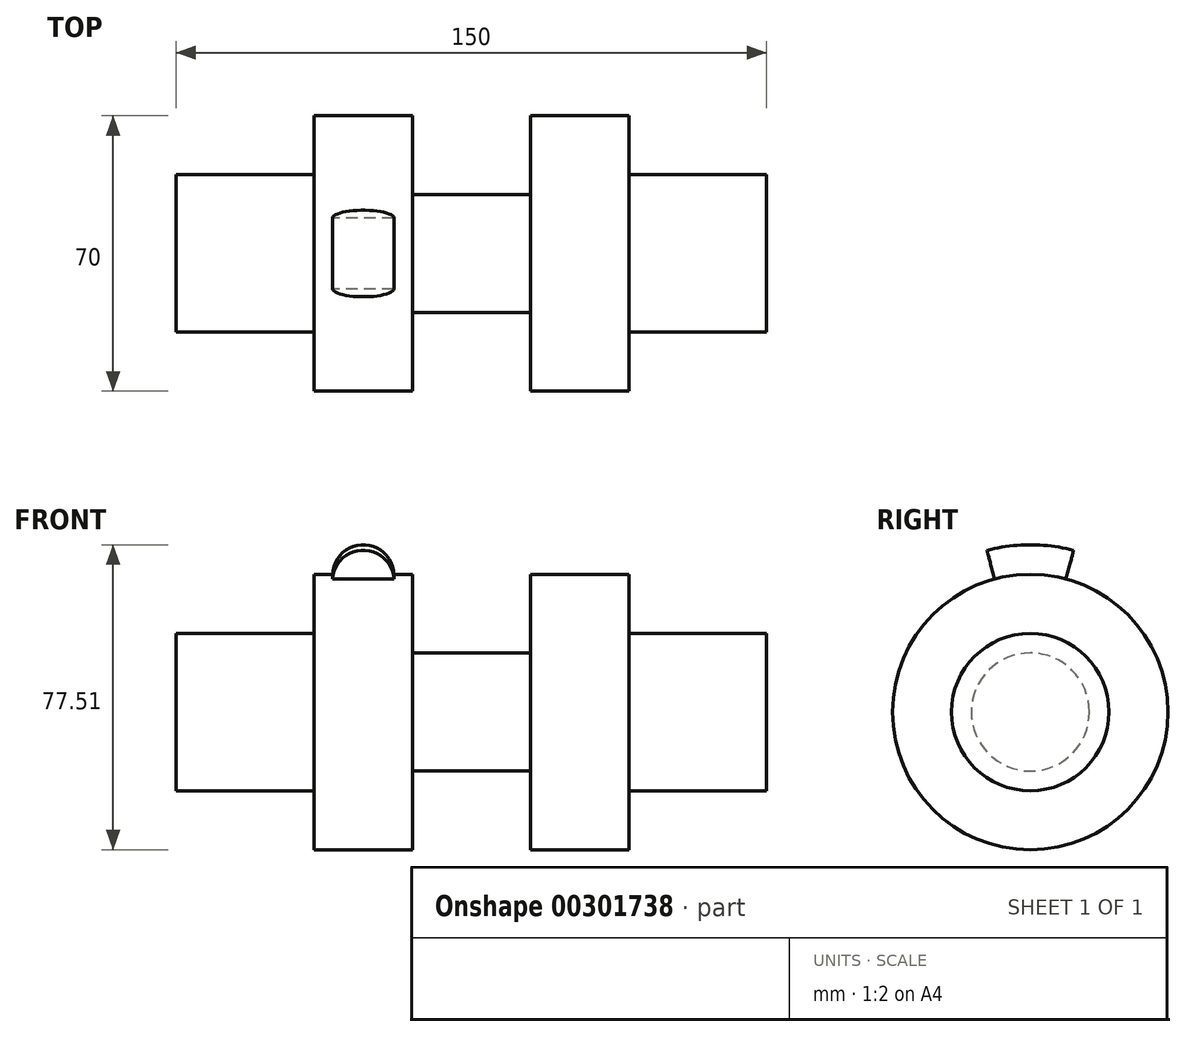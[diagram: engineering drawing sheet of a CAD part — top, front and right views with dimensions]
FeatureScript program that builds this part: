
annotation { "Feature Type Name" : "Feature", "Feature Type Description" : "" }
export const myFeature = defineFeature(function(context is Context, id is Id, definition is map)
    precondition{}
    {
        {
            var Q0;
            Q0=qCreatedBy(makeId("Front.planeOp"),FACE);
            var sketch = newSketch(context, id + "F0", { "sketchPlane" : qUnion([Q0])});
            skLineSegment(sketch, "E0.bottom", {"start": v(0, 0) * mm, "end": v(150, 0) * mm});
            skLineSegment(sketch, "E0.top", {"start": v(35, 35) * mm, "end": v(60, 35) * mm});
            skLineSegment(sketch, "E0.left", {"start": v(0, 0) * mm, "end": v(0, 20) * mm});
            skLineSegment(sketch, "E0.right", {"start": v(150, 0) * mm, "end": v(150, 20) * mm});
            skLineSegment(sketch, "E1.top", {"start": v(0, 20) * mm, "end": v(35, 20) * mm});
            skLineSegment(sketch, "E1.right", {"start": v(35, 35) * mm, "end": v(35, 20) * mm});
            skLineSegment(sketch, "E2.top", {"start": v(60, 15) * mm, "end": v(90, 15) * mm});
            skLineSegment(sketch, "E2.left", {"start": v(60, 35) * mm, "end": v(60, 15) * mm});
            skLineSegment(sketch, "E2.right", {"start": v(90, 35) * mm, "end": v(90, 15) * mm});
            skLineSegment(sketch, "E3.top", {"start": v(115, 20) * mm, "end": v(150, 20) * mm});
            skLineSegment(sketch, "E3.left", {"start": v(115, 35) * mm, "end": v(115, 20) * mm});
            skLineSegment(sketch, "E4.trimOffspring", {"start": v(90, 35) * mm, "end": v(115, 35) * mm});
            skSolve(sketch);
        }
        {
            var Q0;
            Q0=makeQuery(id+"F0.imprint","IMPRINT",FACE,{"disambiguationData":[TD([[makeQuery(id+"F0.imprint","IMPRINT",EDGE,{"derivedFrom":sQuery(id+"F0.wireOp",EDGE,"E0.bottom")}),1.0]])]});
            var Q1;
            Q1=sQuery(id+"F0.wireOp",EDGE,"E0.bottom");
            revolve(context, id + "F1", {"entities" : qUnion([Q0]), "axis" : qUnion([Q1]), "revolveType" : RevolveType.FULL});
        }
        {
            var Q0;
            Q0=qCreatedBy(makeId("Front.planeOp"),FACE);
            var sketch = newSketch(context, id + "F2", { "sketchPlane" : qUnion([Q0])});
            skCircle(sketch, "E5", {"center": v(47.54, 34.74) * mm, "radius": 7.77 * mm});
            skLineSegment(sketch, "E6", {"start": v(0, 0) * mm, "end": v(165.78, 0) * mm});
            skSolve(sketch);
        }
        {
            var Q0;
            Q0 = qSketchRegion(id + "F2", true);
            var Q1;
            Q1=sQuery(id+"F2.wireOp",EDGE,"E6");
            revolve(context, id + "F3", {"operationType" : NewBodyOperationType.ADD, "entities" : qUnion([Q0]), "axis" : qUnion([Q1]), "revolveType" : RevolveType.SYMMETRIC, "angle" : 30 * degree});
        }
    });
